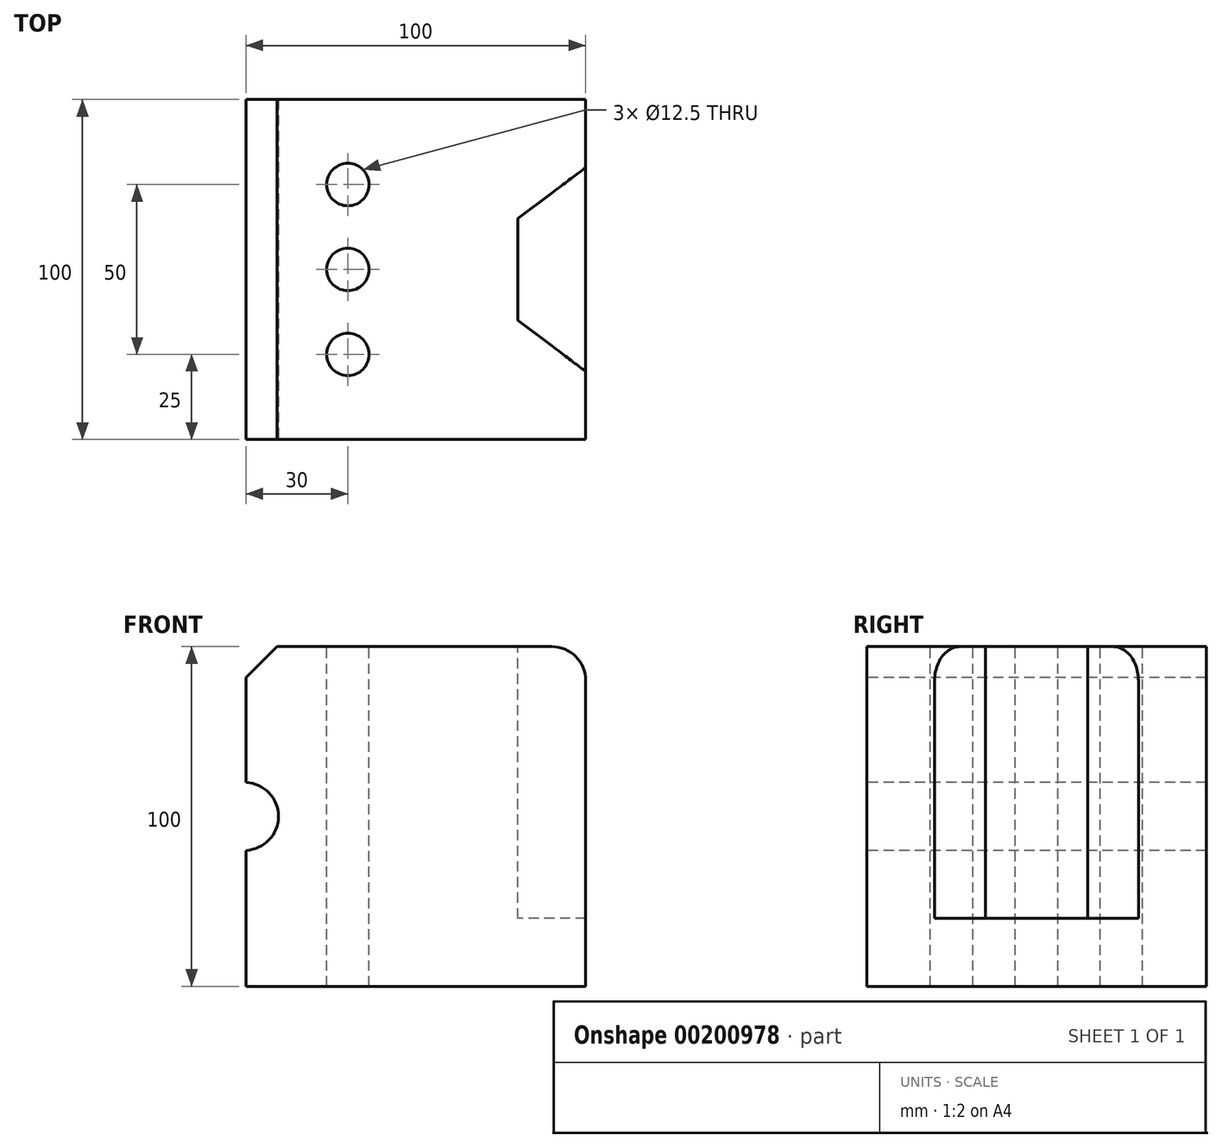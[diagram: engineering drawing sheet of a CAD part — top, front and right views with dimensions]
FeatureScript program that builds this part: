
annotation { "Feature Type Name" : "Feature", "Feature Type Description" : "" }
export const myFeature = defineFeature(function(context is Context, id is Id, definition is map)
    precondition{}
    {
        {
            var Q0;
            Q0=qCreatedBy(makeId("Right.planeOp"),FACE);
            var sketch = newSketch(context, id + "F0", { "sketchPlane" : qUnion([Q0])});
            skLineSegment(sketch, "E0.bottom", {"start": v(50, 50) * mm, "end": v(-50, 50) * mm});
            skLineSegment(sketch, "E0.top", {"start": v(50, -50) * mm, "end": v(-50, -50) * mm});
            skLineSegment(sketch, "E0.left", {"start": v(50, 50) * mm, "end": v(50, -50) * mm});
            skLineSegment(sketch, "E0.right", {"start": v(-50, 50) * mm, "end": v(-50, -50) * mm});
            skPoint(sketch, "E0.middle", {"position": v(0, 0) * mm});
            skSolve(sketch);
        }
        {
            var Q0;
            Q0 = qSketchRegion(id + "F0", true);
            extrude(context, id + "F1", {"entities" : qUnion([Q0]), "endBound" : BoundingType.SYMMETRIC, "depth" : 100 * mm});
        }
        {
            var Q0;
            Q0=qCreatedBy(makeId("Front.planeOp"),FACE);
            var sketch = newSketch(context, id + "F2", { "sketchPlane" : qUnion([Q0])});
            skCircle(sketch, "E1", {"center": v(-50.43, 0) * mm, "radius": 10 * mm});
            skLineSegment(sketch, "E2", {"start": v(-50.43, 50.43) * mm, "end": v(-40.43, 50.43) * mm});
            skLineSegment(sketch, "E3", {"start": v(-40.43, 50.43) * mm, "end": v(-50.43, 40.43) * mm});
            skLineSegment(sketch, "E4", {"start": v(-50.43, 40.43) * mm, "end": v(-50.43, 50.43) * mm});
            skSolve(sketch);
        }
        {
            var Q0;
            Q0 = qSketchRegion(id + "F2", true);
            extrude(context, id + "F3", {"entities" : qUnion([Q0]), "operationType" : NewBodyOperationType.REMOVE, "endBound" : BoundingType.SYMMETRIC, "oppositeDirection" : true, "depth" : 100 * mm});
        }
        {
            var Q0;
            Q0=makeQuery(id+"F1.opExtrude","SWEPT_FACE",FACE,{"disambiguationData":[OSD([sQuery(id+"F0.wireOp",EDGE,"E0.bottom")])]});
            var sketch = newSketch(context, id + "F4", { "sketchPlane" : qUnion([Q0])});
            skCircle(sketch, "E5", {"center": v(-20, 25) * mm, "radius": 6.25 * mm});
            skCircle(sketch, "E6", {"center": v(-20, 0) * mm, "radius": 6.25 * mm});
            skCircle(sketch, "E7", {"center": v(-20, -25) * mm, "radius": 6.25 * mm});
            skLineSegment(sketch, "E8.2", {"start": v(50, -30) * mm, "end": v(30, -15) * mm});
            skLineSegment(sketch, "E8.3", {"start": v(30, -15) * mm, "end": v(30, 15) * mm});
            skLineSegment(sketch, "E8.4", {"start": v(30, 15) * mm, "end": v(50, 30) * mm});
            skLineSegment(sketch, "E9", {"start": v(50, 30) * mm, "end": v(50, -30) * mm});
            skSolve(sketch);
        }
        {
            var Q0;
            Q0=makeQuery(id+"F4.imprint","IMPRINT",FACE,{"disambiguationData":[TD([[makeQuery(id+"F4.imprint","IMPRINT",EDGE,{"derivedFrom":sQuery(id+"F4.wireOp",EDGE,"E5")}),1.0]])]});
            var Q1;
            Q1=makeQuery(id+"F4.imprint","IMPRINT",FACE,{"disambiguationData":[TD([[makeQuery(id+"F4.imprint","IMPRINT",EDGE,{"derivedFrom":sQuery(id+"F4.wireOp",EDGE,"E6")}),1.0]])]});
            var Q2;
            Q2=makeQuery(id+"F4.imprint","IMPRINT",FACE,{"disambiguationData":[TD([[makeQuery(id+"F4.imprint","IMPRINT",EDGE,{"derivedFrom":sQuery(id+"F4.wireOp",EDGE,"E7")}),1.0]])]});
            extrude(context, id + "F5", {"entities" : qUnion([Q0, Q1, Q2]), "operationType" : NewBodyOperationType.REMOVE, "oppositeDirection" : true, "depth" : 100 * mm});
        }
        {
            var Q0;
            Q0=makeQuery(id+"F4.imprint","IMPRINT",FACE,{"disambiguationData":[TD([[makeQuery(id+"F4.imprint","IMPRINT",EDGE,{"derivedFrom":sQuery(id+"F4.wireOp",EDGE,"E8.2")}),-1.0]])]});
            extrude(context, id + "F6", {"entities" : qUnion([Q0]), "operationType" : NewBodyOperationType.REMOVE, "oppositeDirection" : true, "depth" : 80 * mm});
        }
        {
            var Q0;
            {var subQ0=sQuery(id+"F0.wireOp",EDGE,"E0.bottom");var subQ1=sQuery(id+"F0.wireOp",EDGE,"E0.left");Q0=makeQuery(id+"F6.boolean.opBoolean","SPLIT",EDGE,{"disambiguationData":[TD([makeQuery(id+"F1.opExtrude","SWEPT_FACE",FACE,{"disambiguationData":[OSD([subQ1])]})])],"derivedFrom":makeQuery(id+"F1.opExtrude","CAP_EDGE",EDGE,{"disambiguationData":[OSD([subQ0])],"isStart":false})});}
            fillet(context, id + "F7", {"entities" : qUnion([Q0]), "radius" : 10 * mm, "tangentPropagation" : true, "allowEdgeOverflow" : false});
        }
        {
            var Q0;
            {var subQ0=sQuery(id+"F0.wireOp",EDGE,"E0.bottom");var subQ1=sQuery(id+"F0.wireOp",EDGE,"E0.right");Q0=makeQuery(id+"F6.boolean.opBoolean","SPLIT",EDGE,{"disambiguationData":[TD([makeQuery(id+"F1.opExtrude","SWEPT_FACE",FACE,{"disambiguationData":[OSD([subQ1])]})])],"derivedFrom":makeQuery(id+"F1.opExtrude","CAP_EDGE",EDGE,{"disambiguationData":[OSD([subQ0])],"isStart":false})});}
            fillet(context, id + "F8", {"entities" : qUnion([Q0]), "radius" : 10 * mm, "tangentPropagation" : true, "allowEdgeOverflow" : false});
        }
    });
